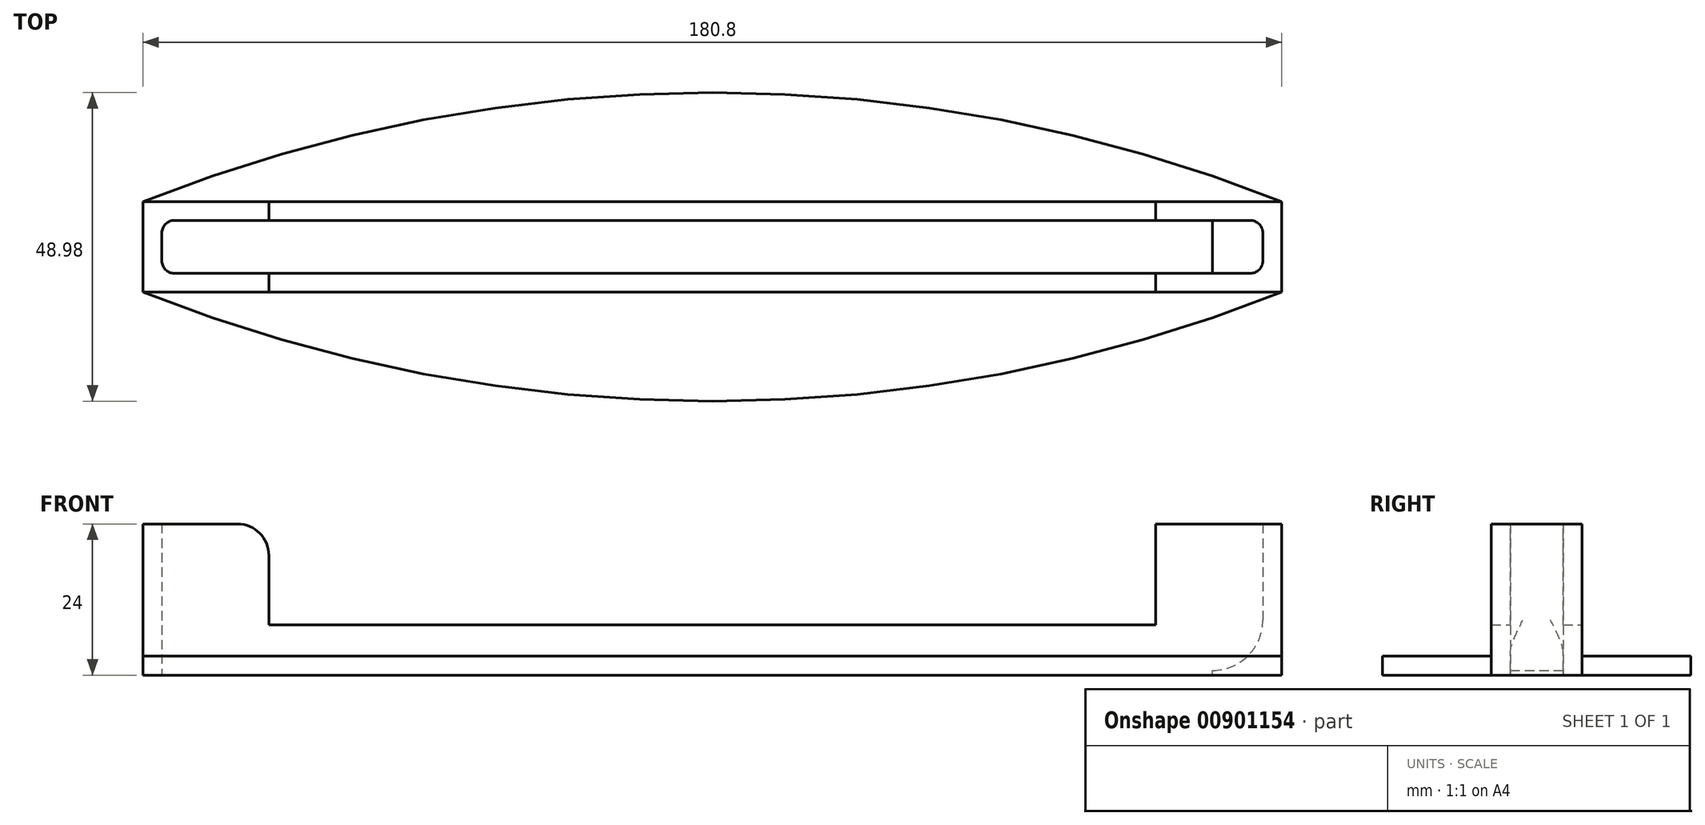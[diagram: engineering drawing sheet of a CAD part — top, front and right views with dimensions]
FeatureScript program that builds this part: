
annotation { "Feature Type Name" : "Feature", "Feature Type Description" : "" }
export const myFeature = defineFeature(function(context is Context, id is Id, definition is map)
    precondition{}
    {
        {
            assignVariable(context, id + "F0", {"name" : "gap", "anyValue" : .1});
        }
        {
            var Q0;
            Q0=qCreatedBy(makeId("Top.planeOp"),FACE);
            var sketch = newSketch(context, id + "F1", { "sketchPlane" : qUnion([Q0])});
            skLineSegment(sketch, "E0.bottom", {"start": v(87.4, -4.2) * mm, "end": v(-87.4, -4.2) * mm});
            skLineSegment(sketch, "E0.top", {"start": v(87.4, 4.2) * mm, "end": v(-87.4, 4.2) * mm});
            skLineSegment(sketch, "E0.left", {"start": v(87.4, -4.2) * mm, "end": v(87.4, 4.2) * mm});
            skLineSegment(sketch, "E0.right", {"start": v(-87.4, -4.2) * mm, "end": v(-87.4, 4.2) * mm});
            skPoint(sketch, "E0.middle", {"position": v(0, 0) * mm});
            skLineSegment(sketch, "E1.bottom", {"start": v(90.4, -7.2) * mm, "end": v(-90.4, -7.2) * mm});
            skLineSegment(sketch, "E1.top", {"start": v(90.4, 7.2) * mm, "end": v(-90.4, 7.2) * mm});
            skLineSegment(sketch, "E1.left", {"start": v(90.4, -7.2) * mm, "end": v(90.4, 7.2) * mm});
            skLineSegment(sketch, "E1.right", {"start": v(-90.4, -7.2) * mm, "end": v(-90.4, 7.2) * mm});
            skSolve(sketch);
        }
        {
            var Q0;
            Q0=qSketchRegion(id+"F1",true);
            extrude(context, id + "F2", {"entities" : qUnion([Q0]), "depth" : 24 * mm, "offsetDistance" : 25 * mm});
        }
        {
            var Q0;
            Q0=makeQuery(id+"F2.opExtrude","SWEPT_EDGE",EDGE,{"disambiguationData":[OSD([sQuery(id+"F1.wireOp",EDGE,"E0.bottom"),sQuery(id+"F1.wireOp",EDGE,"E0.left")])]});
            var Q1;
            Q1=makeQuery(id+"F2.opExtrude","SWEPT_EDGE",EDGE,{"disambiguationData":[OSD([sQuery(id+"F1.wireOp",EDGE,"E0.top"),sQuery(id+"F1.wireOp",EDGE,"E0.left")])]});
            var Q2;
            Q2=makeQuery(id+"F2.opExtrude","SWEPT_EDGE",EDGE,{"disambiguationData":[OSD([sQuery(id+"F1.wireOp",EDGE,"E0.bottom"),sQuery(id+"F1.wireOp",EDGE,"E0.right")])]});
            var Q3;
            Q3=makeQuery(id+"F2.opExtrude","SWEPT_EDGE",EDGE,{"disambiguationData":[OSD([sQuery(id+"F1.wireOp",EDGE,"E0.top"),sQuery(id+"F1.wireOp",EDGE,"E0.right")])]});
            fillet(context, id + "F3", {"entities" : qUnion([Q0, Q1, Q2, Q3]), "radius" : 2 * mm, "tangentPropagation" : true, "allowEdgeOverflow" : false});
        }
        {
            var Q0;
            Q0=qCreatedBy(makeId("Front.planeOp"),FACE);
            var sketch = newSketch(context, id + "F4", { "sketchPlane" : qUnion([Q0])});
            skArc(sketch, "E2", {"start": v(79.4, 0.75) * mm, "mid": v(85.06, 3.1) * mm, "end": v(87.4, 8.75) * mm});
            skLineSegment(sketch, "E3", {"start": v(87.4, 8.75) * mm, "end": v(90.4, 8.75) * mm});
            skLineSegment(sketch, "E4", {"start": v(90.4, 8.75) * mm, "end": v(90.4, 0) * mm});
            skLineSegment(sketch, "E5", {"start": v(79.4, 0.75) * mm, "end": v(79.4, 0) * mm});
            skLineSegment(sketch, "E6", {"start": v(79.4, 0) * mm, "end": v(90.4, 0) * mm});
            skSolve(sketch);
        }
        {
            var Q0;
            Q0=qSketchRegion(id+"F4",true);
            extrude(context, id + "F5", {"entities" : qUnion([Q0]), "operationType" : NewBodyOperationType.ADD, "endBound" : BoundingType.SYMMETRIC, "depth" : (8.5 + (2 * getVariable(context, 'gap'))) * mm, "offsetDistance" : 25 * mm});
        }
        {
            var Q0;
            Q0=makeQuery(id+"F2.opExtrude","CAP_FACE",FACE,{"disambiguationData":[OSD([sQuery(id+"F1.wireOp",EDGE,"E0.bottom"),sQuery(id+"F1.wireOp",EDGE,"E0.top"),sQuery(id+"F1.wireOp",EDGE,"E0.left"),sQuery(id+"F1.wireOp",EDGE,"E0.right"),sQuery(id+"F1.wireOp",EDGE,"E1.bottom"),sQuery(id+"F1.wireOp",EDGE,"E1.top"),sQuery(id+"F1.wireOp",EDGE,"E1.left"),sQuery(id+"F1.wireOp",EDGE,"E1.right")])],"isStart":false});
            var sketch = newSketch(context, id + "F6", { "sketchPlane" : qUnion([Q0])});
            skLineSegment(sketch, "E7.bottom", {"start": v(-70.4, -7.2) * mm, "end": v(70.4, -7.2) * mm});
            skLineSegment(sketch, "E7.top", {"start": v(-70.4, 7.2) * mm, "end": v(70.4, 7.2) * mm});
            skLineSegment(sketch, "E7.left", {"start": v(-70.4, -7.2) * mm, "end": v(-70.4, 7.2) * mm});
            skLineSegment(sketch, "E7.right", {"start": v(70.4, -7.2) * mm, "end": v(70.4, 7.2) * mm});
            skSolve(sketch);
        }
        {
            var Q0;
            Q0=qSketchRegion(id+"F6",true);
            extrude(context, id + "F7", {"entities" : qUnion([Q0]), "operationType" : NewBodyOperationType.REMOVE, "oppositeDirection" : true, "depth" : 16 * mm, "offsetDistance" : 25 * mm});
        }
        {
            var Q0;
            {var subQ1=sQuery(id+"F1.wireOp",EDGE,"E0.top");var subQ2=sQuery(id+"F6.wireOp",EDGE,"E7.left");Q0=makeQuery(id+"F7.boolean.opBoolean","COPY",EDGE,{"disambiguationData":[TD([makeQuery(id+"F2.opExtrude","SWEPT_FACE",FACE,{"disambiguationData":[OSD([subQ1])]})])],"derivedFrom":makeQuery(id+"F7.opExtrude","CAP_EDGE",EDGE,{"disambiguationData":[OSD([subQ2])],"isStart":true})});}
            var Q1;
            {var subQ0=sQuery(id+"F1.wireOp",EDGE,"E0.bottom");var subQ1=sQuery(id+"F6.wireOp",EDGE,"E7.left");Q1=makeQuery(id+"F7.boolean.opBoolean","COPY",EDGE,{"disambiguationData":[TD([makeQuery(id+"F2.opExtrude","SWEPT_FACE",FACE,{"disambiguationData":[OSD([subQ0])]})])],"derivedFrom":makeQuery(id+"F7.opExtrude","CAP_EDGE",EDGE,{"disambiguationData":[OSD([subQ1])],"isStart":true})});}
            var Q2;
            {var subQ1=sQuery(id+"F1.wireOp",EDGE,"E0.top");var subQ2=sQuery(id+"F6.wireOp",EDGE,"E7.right");Q2=makeQuery(id+"F7.boolean.opBoolean","COPY",EDGE,{"disambiguationData":[TD([makeQuery(id+"F2.opExtrude","SWEPT_FACE",FACE,{"disambiguationData":[OSD([subQ1])]})])],"derivedFrom":makeQuery(id+"F7.opExtrude","CAP_EDGE",EDGE,{"disambiguationData":[OSD([subQ2])],"isStart":true})});}
            var Q3;
            {var subQ0=sQuery(id+"F1.wireOp",EDGE,"E0.bottom");var subQ2=sQuery(id+"F6.wireOp",EDGE,"E7.right");Q3=makeQuery(id+"F7.boolean.opBoolean","COPY",EDGE,{"disambiguationData":[TD([makeQuery(id+"F2.opExtrude","SWEPT_FACE",FACE,{"disambiguationData":[OSD([subQ0])]})])],"derivedFrom":makeQuery(id+"F7.opExtrude","CAP_EDGE",EDGE,{"disambiguationData":[OSD([subQ2])],"isStart":true})});}
            fillet(context, id + "F8", {"entities" : qUnion([Q0, Q1, Q2, Q3]), "radius" : 5 * mm, "tangentPropagation" : true, "allowEdgeOverflow" : false});
        }
        {
            var Q0;
            Q0=qCreatedBy(makeId("Top.planeOp"),FACE);
            var sketch = newSketch(context, id + "F9", { "sketchPlane" : qUnion([Q0])});
            skArc(sketch, "E8", {"start": v(-90.4, -7.2) * mm, "mid": v(0, -24.49) * mm, "end": v(90.4, -7.2) * mm});
            skArc(sketch, "E9", {"start": v(90.4, 7.2) * mm, "mid": v(0, 24.49) * mm, "end": v(-90.4, 7.2) * mm});
            skLineSegment(sketch, "E10", {"start": v(-90.4, -7.2) * mm, "end": v(90.4, -7.2) * mm});
            skLineSegment(sketch, "E11", {"start": v(-90.4, 7.2) * mm, "end": v(90.4, 7.2) * mm});
            skSolve(sketch);
        }
        {
            var Q0;
            Q0 = qSketchRegion(id + "F9", true);
            extrude(context, id + "F10", {"entities" : qUnion([Q0]), "operationType" : NewBodyOperationType.ADD, "depth" : 3 * mm, "offsetDistance" : 25 * mm});
        }
    });
